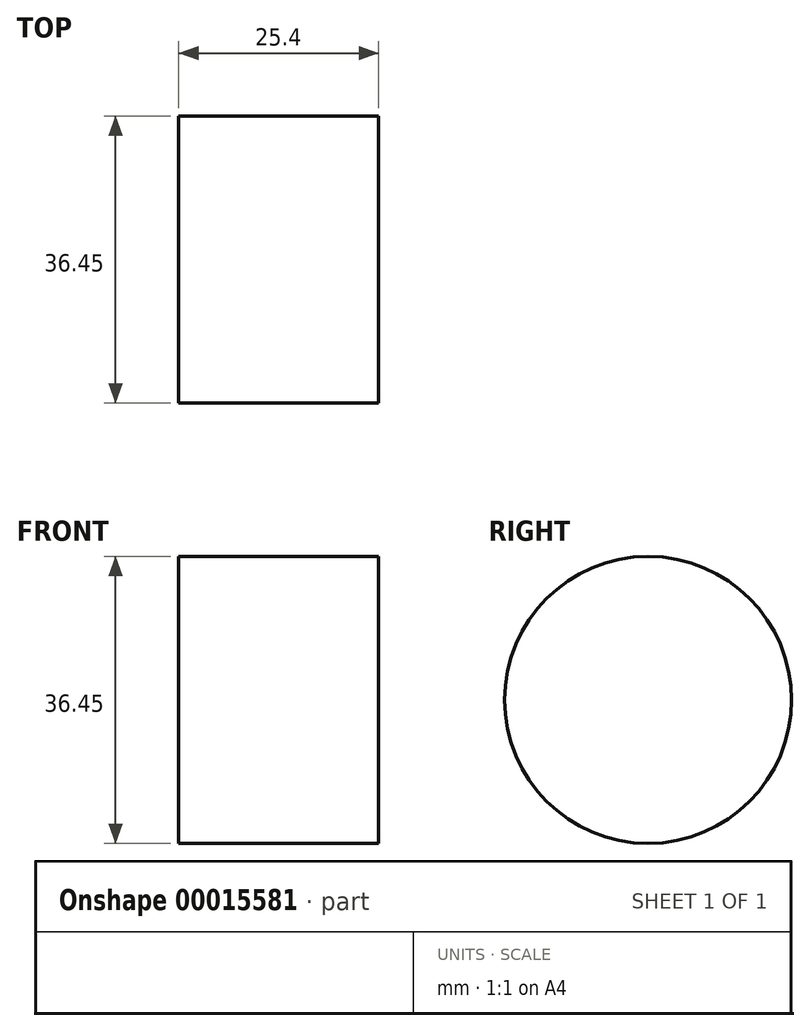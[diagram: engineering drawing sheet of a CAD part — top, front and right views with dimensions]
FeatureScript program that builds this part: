
annotation { "Feature Type Name" : "Feature", "Feature Type Description" : "" }
export const myFeature = defineFeature(function(context is Context, id is Id, definition is map)
    precondition{}
    {
        {
            var Q0;
            Q0=qCreatedBy(makeId("Right.planeOp"),FACE);
            var sketch = newSketch(context, id + "F0", { "sketchPlane" : qUnion([Q0])});
            skCircle(sketch, "E0", {"center": v(37.65, 23.82) * mm, "radius": 18.22 * mm});
            skSolve(sketch);
        }
        {
            var Q0;
            Q0=makeQuery(id+"F0.imprint","IMPRINT",FACE,{"disambiguationData":[TD([[makeQuery(id+"F0.imprint","IMPRINT",EDGE,{"derivedFrom":sQuery(id+"F0.wireOp",EDGE,"E0")}),1.0]])]});
            extrude(context, id + "F1", {"entities" : qUnion([Q0]), "oppositeDirection" : true, "depth" : 25.4 * mm});
        }
    });
